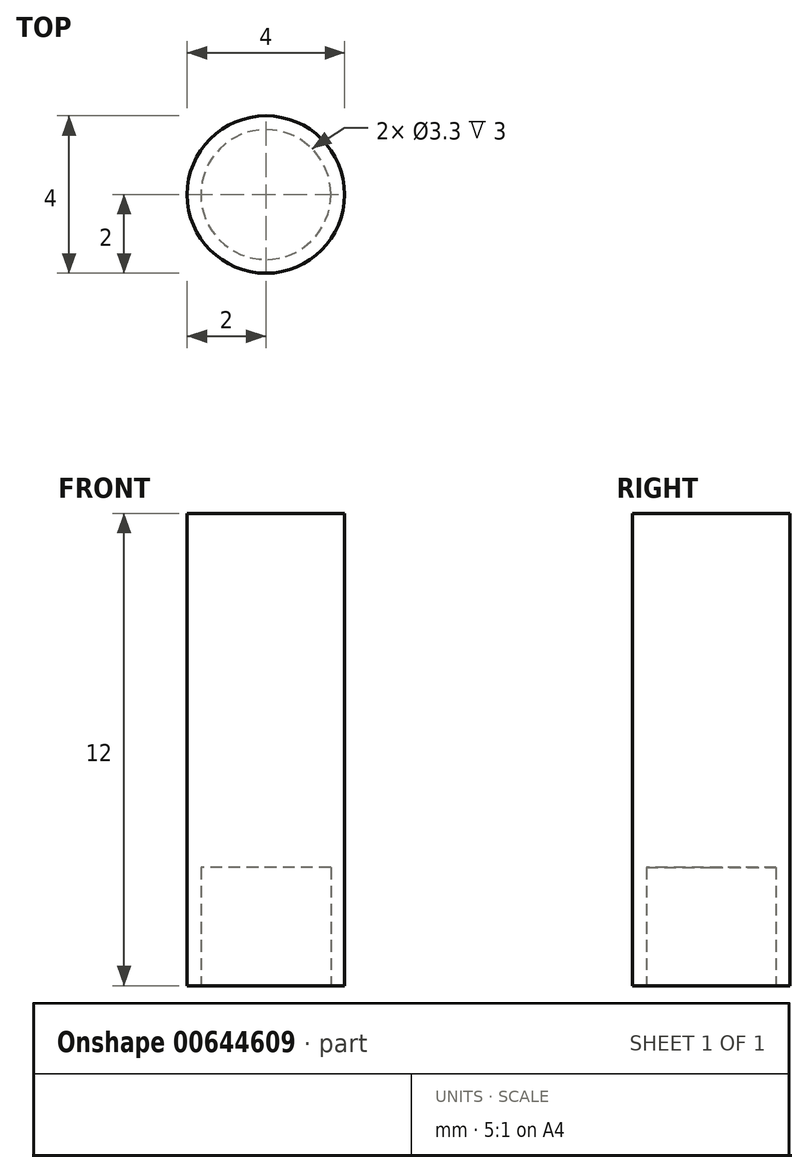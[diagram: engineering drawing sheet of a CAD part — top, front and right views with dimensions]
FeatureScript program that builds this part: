
annotation { "Feature Type Name" : "Feature", "Feature Type Description" : "" }
export const myFeature = defineFeature(function(context is Context, id is Id, definition is map)
    precondition{}
    {
        {
            var Q0;
            Q0=qCreatedBy(makeId("Top.planeOp"),FACE);
            var sketch = newSketch(context, id + "F0", { "sketchPlane" : qUnion([Q0])});
            skCircle(sketch, "E0", {"center": v(0, 0) * mm, "radius": 2 * mm});
            skSolve(sketch);
        }
        {
            var Q0;
            Q0 = qSketchRegion(id + "F0", true);
            extrude(context, id + "F1", {"entities" : qUnion([Q0]), "depth" : 12 * mm, "offsetDistance" : 25.4 * mm});
        }
        {
            var Q0;
            Q0=qCreatedBy(makeId("Top.planeOp"),FACE);
            var sketch = newSketch(context, id + "F2", { "sketchPlane" : qUnion([Q0])});
            skCircle(sketch, "E1", {"center": v(0, 0) * mm, "radius": 1.65 * mm});
            skSolve(sketch);
        }
        {
            var Q0;
            Q0=makeQuery(id+"F2.imprint","IMPRINT",FACE,{"disambiguationData":[TD([[makeQuery(id+"F2.imprint","IMPRINT",EDGE,{"derivedFrom":sQuery(id+"F2.wireOp",EDGE,"E1")}),1.0]])]});
            var Q1;
            Q1=sQuery(id+"F2.wireOp",EDGE,"E1");
            extrude(context, id + "F3", {"entities" : qUnion([Q0]), "operationType" : NewBodyOperationType.REMOVE, "surfaceEntities" : qUnion([Q1]), "depth" : 3 * mm, "offsetDistance" : 25.4 * mm});
        }
    });
